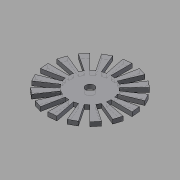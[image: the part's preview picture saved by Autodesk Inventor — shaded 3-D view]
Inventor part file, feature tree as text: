
AUTODESK INVENTOR PART (.ipt)
format: ipt  version: 2015 (Build 190159000, 159)  size: 173,568 bytes
history: native  units: in
note: dims shown in document units (in); Inventor stores cm internally (conversion verified against a paired STEP export)
features: other x3, sketch x1
ambient origin geometry x8: Origin, YZ Plane, XZ Plane, XY Plane, X Axis, Y Axis, Z Axis, Center Point
bodies: Solid1 (feature_tree)
feature tree (4):
  other  "encoder_MIR1.ipt"
  other  "Solid1::encoder_MIR1.ipt"
  other  "TaggingFeature1"
  sketch  "Sketch1"  dims[d0=0.3937in]
